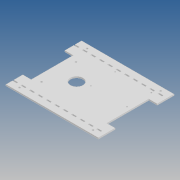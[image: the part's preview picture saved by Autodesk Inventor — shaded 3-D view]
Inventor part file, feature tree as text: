
AUTODESK INVENTOR PART (.ipt)
format: ipt  version: 2020 (Build 240168000, 168)  size: 239,104 bytes
history: native  units: mm
features: extrude x8, sketch x8, other x7, reference x6, mirror x2, pattern_linear x1
ambient origin geometry x8: Origin, YZ Plane, XZ Plane, XY Plane, X Axis, Y Axis, Z Axis, Center Point
bodies: Body1 (feature_tree)
feature tree (32):
  extrude  "Выдавливание12"  Depth=220.0mm TaperAngle=0.0deg
  mirror  "Зеркальное отражение1"
  extrude  "Выдавливание13"  Depth=3.0mm TaperAngle=0.0deg
  extrude  "Выдавливание14"  Depth=10.0mm TaperAngle=0.0deg
  extrude  "Выдавливание15"  Depth=20.0mm
  extrude  "Выдавливание16"  Depth=50.0mm
  pattern_linear  "Прямоуг.массив5"  Count1=10  [1 undecoded]
  mirror  "Зеркальное отражение2"
  sketch  "Эскиз12"
  sketch  "Эскиз13"
  sketch  "Эскиз14"
  reference  "Ссылка9"
  reference  "Ссылка10"
  sketch  "Эскиз15"
  reference  "Ссылка11"
  reference  "Ссылка12"
  reference  "Ссылка13"
  reference  "Ссылка14"
  sketch  "Эскиз16"
  sketch  "Эскиз9"
  sketch  "Эскиз10"
  sketch  "Эскиз11"
  other  "<path> - Electronic box.iam"
  other  "000.100 - Electronic box.iam"
  other  "realsenses_plate_v2.ipt:1"
  other  "realsenses_plate_2:2"
  other  "Jetson nano_fixed:1"
  other  "142-13449-1000-A02_ASM:1"
  other  "142-13449-1000-A02:1"
  extrude  "Выдавливание9"  Depth=10.0mm TaperAngle=0.0deg
  extrude  "Выдавливание10"  Depth=30.0mm
  extrude  "Выдавливание11"  Depth=10.0mm TaperAngle=0.0deg
note: 1 required parameter value undecoded (feature->parameter linkage not recoverable at this tier; creation-order binding heuristic only, values carry confidence <= 0.55)
note: 1 file-system path scrubbed to <path> (originals preserved in map.json)
